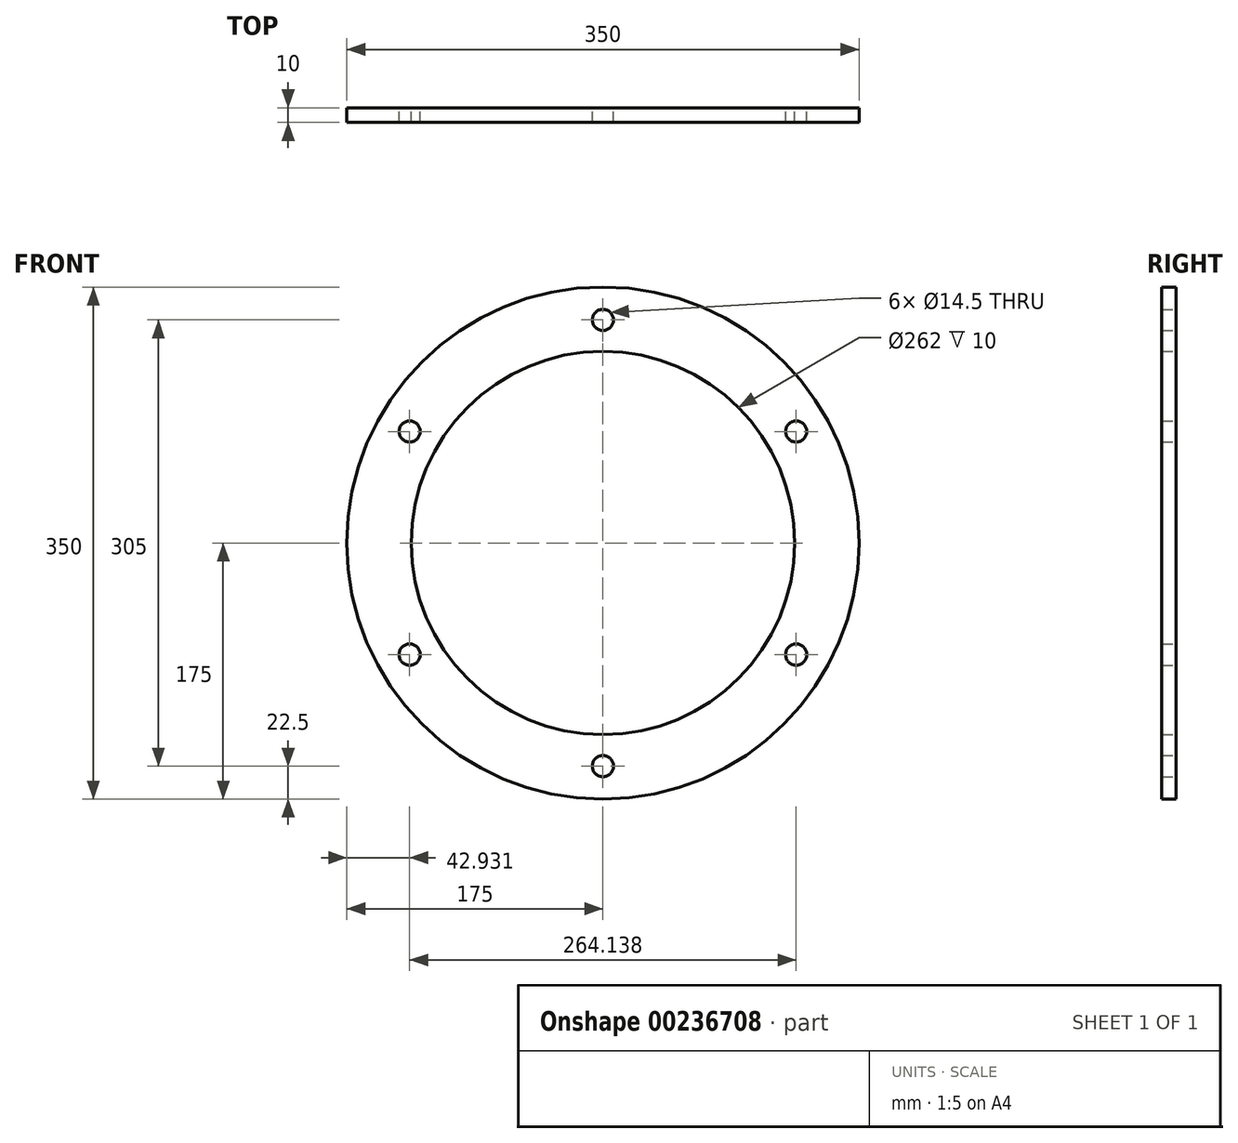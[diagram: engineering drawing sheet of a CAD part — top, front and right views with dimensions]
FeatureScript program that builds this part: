
annotation { "Feature Type Name" : "Feature", "Feature Type Description" : "" }
export const myFeature = defineFeature(function(context is Context, id is Id, definition is map)
    precondition{}
    {
        {
            var Q0;
            Q0=qCreatedBy(makeId("Front.planeOp"),FACE);
            var sketch = newSketch(context, id + "F0", { "sketchPlane" : qUnion([Q0])});
            skCircle(sketch, "E0", {"center": v(0, 0) * mm, "radius": 131 * mm});
            skCircle(sketch, "E1", {"center": v(0, 0) * mm, "radius": 175 * mm});
            skSolve(sketch);
        }
        {
            var Q0;
            Q0 = qSketchRegion(id + "F0", true);
            extrude(context, id + "F1", {"entities" : qUnion([Q0]), "depth" : 10 * mm});
        }
        {
            var Q0;
            Q0=makeQuery(id+"F1.opExtrude","CAP_FACE",FACE,{"disambiguationData":[OSD([sQuery(id+"F0.wireOp",EDGE,"E0"),sQuery(id+"F0.wireOp",EDGE,"E1")])],"isStart":false});
            var sketch = newSketch(context, id + "F2", { "sketchPlane" : qUnion([Q0])});
            skCircle(sketch, "E2", {"center": v(0, 0) * mm, "radius": 152.5 * mm});
            skPoint(sketch, "E3", {"position": v(0, 152.5) * mm});
            skPoint(sketch, "E4.1.0", {"position": v(-132.07, -76.25) * mm});
            skPoint(sketch, "E4.2.0", {"position": v(132.07, -76.25) * mm});
            skPoint(sketch, "E5.1.0", {"position": v(0, -152.5) * mm});
            skPoint(sketch, "E5.3.0", {"position": v(132.07, 76.25) * mm});
            skPoint(sketch, "E5.5.0", {"position": v(-132.07, 76.25) * mm});
            skSolve(sketch);
        }
        {
            var Q0;
            Q0=sQuery(id+"F2.wireOp",VERTEX,"E3");
            var Q1;
            Q1=sQuery(id+"F2.wireOp",VERTEX,"E5.5.0");
            var Q2;
            Q2=sQuery(id+"F2.wireOp",VERTEX,"E4.1.0");
            var Q3;
            Q3=sQuery(id+"F2.wireOp",VERTEX,"E5.1.0");
            var Q4;
            Q4=sQuery(id+"F2.wireOp",VERTEX,"E4.2.0");
            var Q5;
            Q5=sQuery(id+"F2.wireOp",VERTEX,"E5.3.0");
            var Q6;
            Q6=makeQuery(id+"F1.opExtrude","SWEPT_BODY",BODY,{"disambiguationData":[OSD([sQuery(id+"F0.wireOp",EDGE,"E0"),sQuery(id+"F0.wireOp",EDGE,"E1")])]});
            hole(context, id + "F3", {"style" : HoleStyle.SIMPLE, "endStyle" : HoleEndStyle.THROUGH, "standardTappedOrClearance" : lookupTablePath({ "standard" : "ISO", "size" : "14.5", "type" : "Drilled" }), "standardBlindInLast" : lookupTablePath({ "standard" : "ISO", "size" : "14.5", "type" : "Drilled" }), "holeDiameter" : 14.5 * mm, "tappedDepth" : 12 * mm, "tapClearance" : 3, "locations" : qUnion([Q0, Q1, Q2, Q3, Q4, Q5]), "scope" : qUnion([Q6])});
        }
    });
